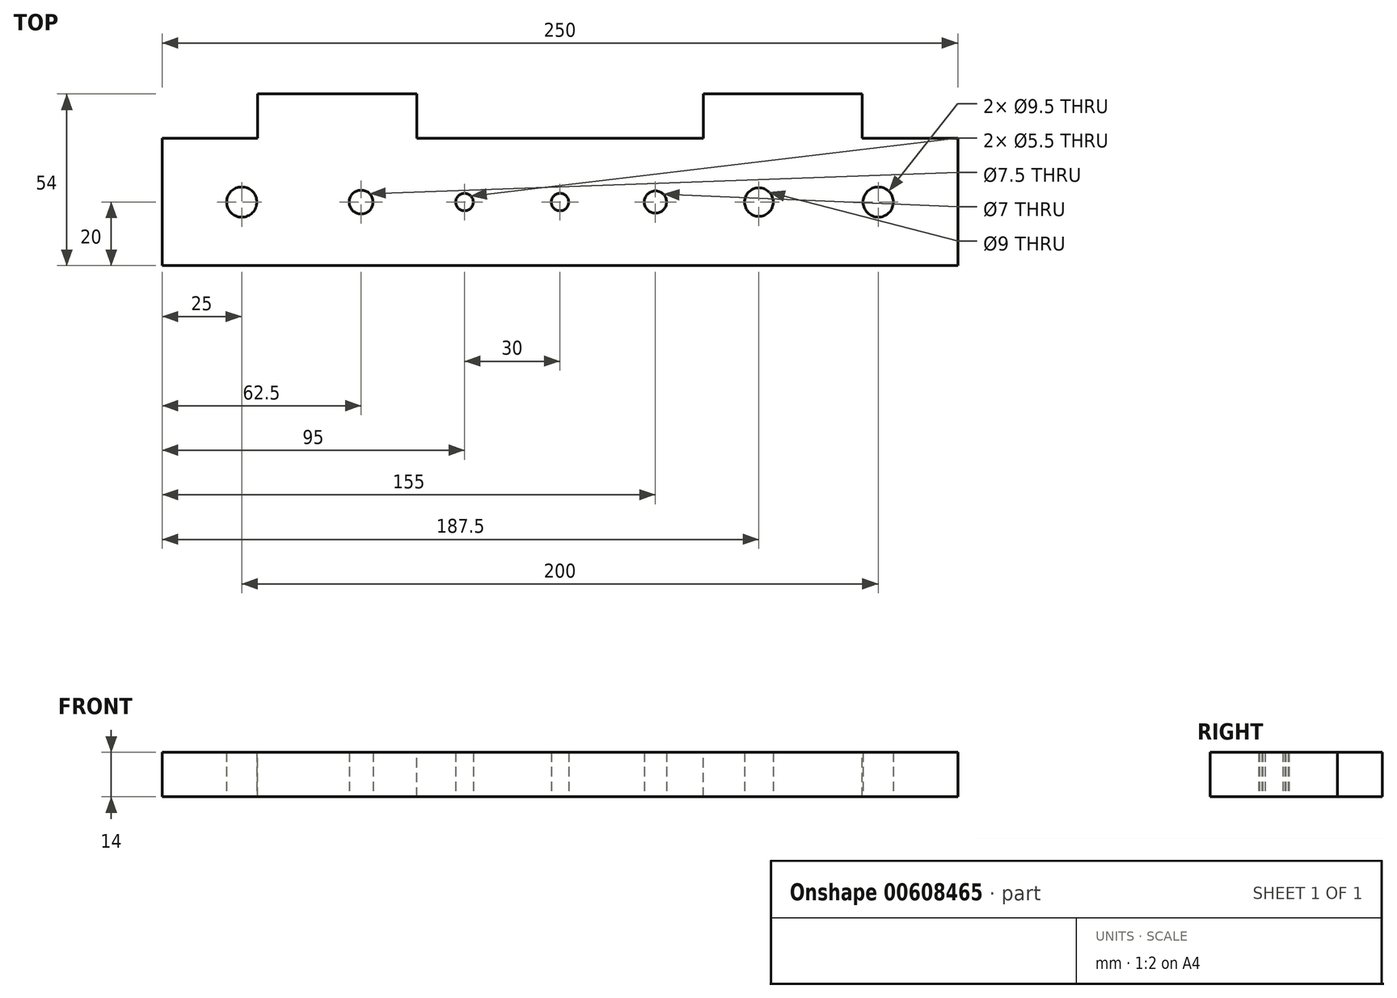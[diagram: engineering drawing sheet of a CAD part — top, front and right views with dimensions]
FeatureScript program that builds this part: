
annotation { "Feature Type Name" : "Feature", "Feature Type Description" : "" }
export const myFeature = defineFeature(function(context is Context, id is Id, definition is map)
    precondition{}
    {
        {
            var Q0;
            Q0=qCreatedBy(makeId("Top.planeOp"),FACE);
            var sketch = newSketch(context, id + "F0", { "sketchPlane" : qUnion([Q0])});
            skLineSegment(sketch, "E0.bottom", {"start": v(-125, 0) * mm, "end": v(125, 0) * mm});
            skLineSegment(sketch, "E0.top", {"start": v(-125, -40) * mm, "end": v(125, -40) * mm});
            skLineSegment(sketch, "E0.left", {"start": v(-125, 0) * mm, "end": v(-125, -40) * mm});
            skLineSegment(sketch, "E0.right", {"start": v(125, 0) * mm, "end": v(125, -40) * mm});
            skPoint(sketch, "E1", {"position": v(0, 0) * mm});
            skPoint(sketch, "E2", {"position": v(125, -20) * mm});
            skCircle(sketch, "E3", {"center": v(-100, -20) * mm, "radius": 4.75 * mm});
            skCircle(sketch, "E4", {"center": v(-62.5, -20) * mm, "radius": 3.75 * mm});
            skCircle(sketch, "E5", {"center": v(-30, -20) * mm, "radius": 2.75 * mm});
            skCircle(sketch, "E6", {"center": v(0, -20) * mm, "radius": 2.75 * mm});
            skCircle(sketch, "E7", {"center": v(30, -20) * mm, "radius": 3.5 * mm});
            skCircle(sketch, "E8", {"center": v(62.5, -20) * mm, "radius": 4.5 * mm});
            skCircle(sketch, "E9", {"center": v(100, -20) * mm, "radius": 4.75 * mm});
            skLineSegment(sketch, "E10", {"start": v(-120, -20) * mm, "end": v(-80, -20) * mm, "construction": true});
            skLineSegment(sketch, "E11", {"start": v(-80, -20) * mm, "end": v(-45, -20) * mm, "construction": true});
            skLineSegment(sketch, "E12", {"start": v(-45, -20) * mm, "end": v(-15, -20) * mm, "construction": true});
            skLineSegment(sketch, "E13", {"start": v(-15, -20) * mm, "end": v(15, -20) * mm, "construction": true});
            skLineSegment(sketch, "E14", {"start": v(15, -20) * mm, "end": v(45, -20) * mm, "construction": true});
            skLineSegment(sketch, "E15", {"start": v(45, -20) * mm, "end": v(80, -20) * mm, "construction": true});
            skLineSegment(sketch, "E16", {"start": v(80, -20) * mm, "end": v(120, -20) * mm, "construction": true});
            skPoint(sketch, "E17", {"position": v(-125, -20) * mm});
            skLineSegment(sketch, "E18", {"start": v(-125, -20) * mm, "end": v(-120, -20) * mm, "construction": true});
            skLineSegment(sketch, "E19", {"start": v(120, -20) * mm, "end": v(125, -20) * mm, "construction": true});
            skSolve(sketch);
        }
        {
            var Q0;
            Q0=makeQuery(id+"F0.imprint","IMPRINT",FACE,{"disambiguationData":[TD([[makeQuery(id+"F0.imprint","IMPRINT",EDGE,{"derivedFrom":sQuery(id+"F0.wireOp",EDGE,"E0.bottom")}),-1.0]])]});
            extrude(context, id + "F1", {"entities" : qUnion([Q0]), "depth" : 14 * mm, "offsetDistance" : 25 * mm});
        }
        {
            var Q0;
            Q0=makeQuery(id+"F1.opExtrude","SWEPT_FACE",FACE,{"disambiguationData":[OSD([sQuery(id+"F0.wireOp",EDGE,"E0.bottom")])]});
            var sketch = newSketch(context, id + "F2", { "sketchPlane" : qUnion([Q0])});
            skLineSegment(sketch, "E20.bottom", {"start": v(95, 0) * mm, "end": v(45, 0) * mm});
            skLineSegment(sketch, "E20.top", {"start": v(95, 14) * mm, "end": v(45, 14) * mm});
            skLineSegment(sketch, "E20.left", {"start": v(95, 0) * mm, "end": v(95, 14) * mm});
            skLineSegment(sketch, "E20.right", {"start": v(45, 0) * mm, "end": v(45, 14) * mm});
            skLineSegment(sketch, "E21.MirrorCS", {"start": v(-95, 0) * mm, "end": v(-45, 0) * mm});
            skLineSegment(sketch, "E22.MirrorCS", {"start": v(-95, 14) * mm, "end": v(-45, 14) * mm});
            skLineSegment(sketch, "E23.MirrorCS", {"start": v(-45, 0) * mm, "end": v(-45, 14) * mm});
            skLineSegment(sketch, "E24.MirrorCS", {"start": v(-95, 0) * mm, "end": v(-95, 14) * mm});
            skSolve(sketch);
        }
        {
            var Q0;
            Q0=makeQuery(id+"F2.imprint","IMPRINT",FACE,{"disambiguationData":[TD([[makeQuery(id+"F2.imprint","IMPRINT",EDGE,{"derivedFrom":sQuery(id+"F2.wireOp",EDGE,"E20.bottom")}),-1.0]])]});
            var Q1;
            Q1=makeQuery(id+"F2.imprint","IMPRINT",FACE,{"disambiguationData":[TD([[makeQuery(id+"F2.imprint","IMPRINT",EDGE,{"derivedFrom":sQuery(id+"F2.wireOp",EDGE,"E21.MirrorCS")}),-1.0]])]});
            extrude(context, id + "F3", {"entities" : qUnion([Q0, Q1]), "operationType" : NewBodyOperationType.ADD, "depth" : 14 * mm, "offsetDistance" : 25 * mm});
        }
    });
